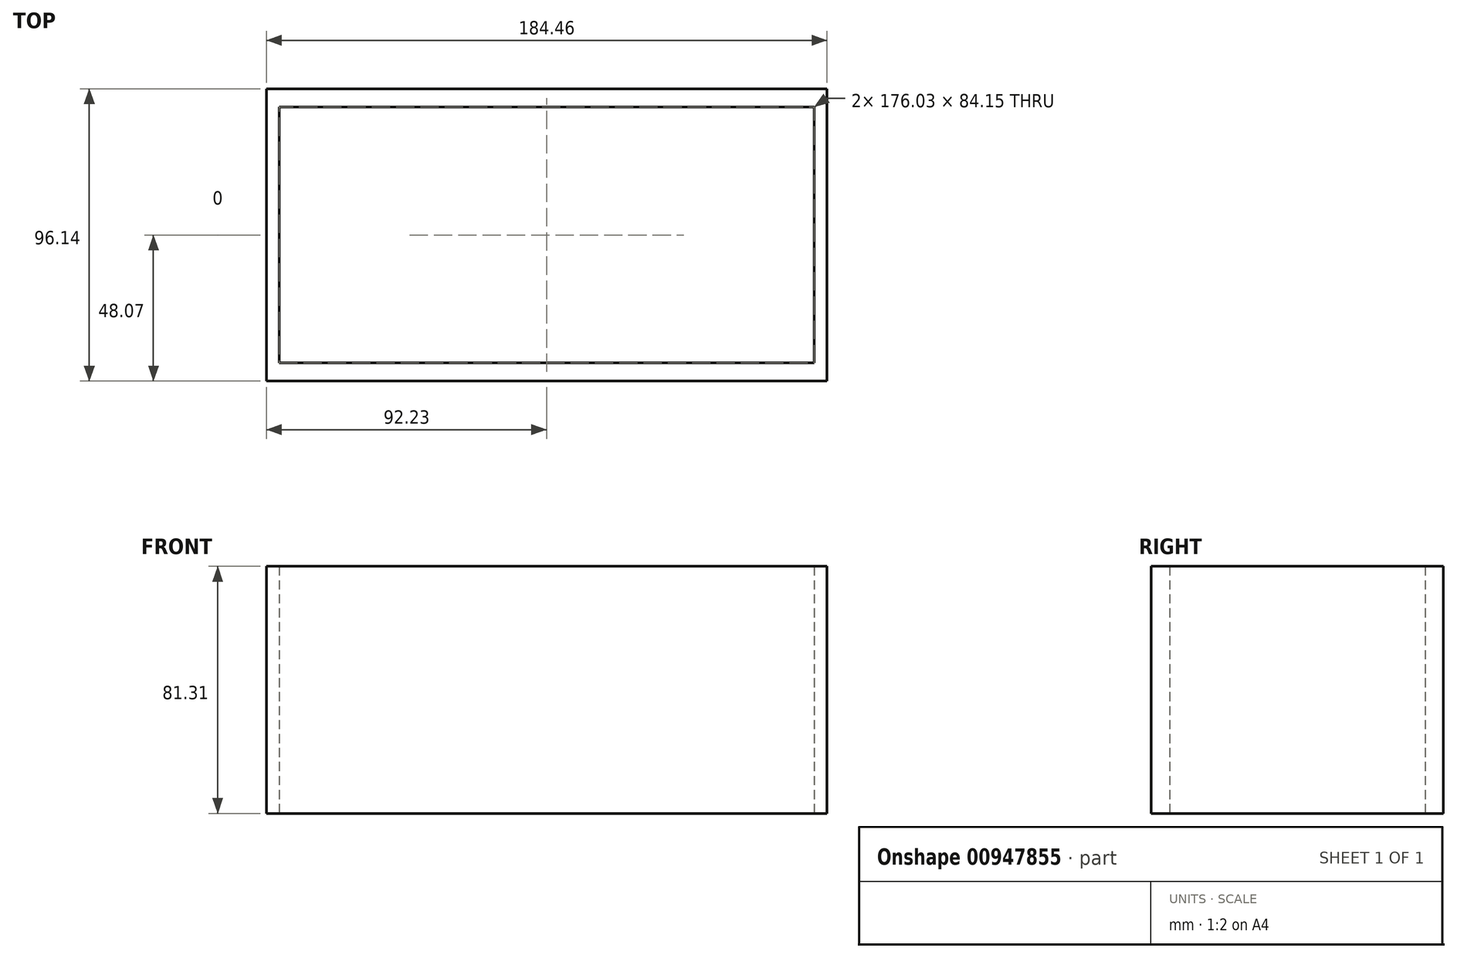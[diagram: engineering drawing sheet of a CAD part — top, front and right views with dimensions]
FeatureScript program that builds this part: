
annotation { "Feature Type Name" : "Feature", "Feature Type Description" : "" }
export const myFeature = defineFeature(function(context is Context, id is Id, definition is map)
    precondition{}
    {
        {
            var Q0;
            Q0=qCreatedBy(makeId("Top.planeOp"),FACE);
            var sketch = newSketch(context, id + "F0", { "sketchPlane" : qUnion([Q0])});
            skLineSegment(sketch, "E0.bottom", {"start": v(92.23, 48.07) * mm, "end": v(-92.23, 48.07) * mm});
            skLineSegment(sketch, "E0.top", {"start": v(92.23, -48.07) * mm, "end": v(-92.23, -48.07) * mm});
            skLineSegment(sketch, "E0.left", {"start": v(92.23, 48.07) * mm, "end": v(92.23, -48.07) * mm});
            skLineSegment(sketch, "E0.right", {"start": v(-92.23, 48.07) * mm, "end": v(-92.23, -48.07) * mm});
            skPoint(sketch, "E0.middle", {"position": v(0, 0) * mm});
            skSolve(sketch);
        }
        {
            var Q0;
            Q0 = qSketchRegion(id + "F0", true);
            var sketch = newSketch(context, id + "F1", { "sketchPlane" : qUnion([Q0])});
            skLineSegment(sketch, "E1.bottom", {"start": v(88.02, 42.08) * mm, "end": v(-88.02, 42.08) * mm});
            skLineSegment(sketch, "E1.top", {"start": v(88.02, -42.08) * mm, "end": v(-88.02, -42.08) * mm});
            skLineSegment(sketch, "E1.left", {"start": v(88.02, 42.08) * mm, "end": v(88.02, -42.08) * mm});
            skLineSegment(sketch, "E1.right", {"start": v(-88.02, 42.08) * mm, "end": v(-88.02, -42.08) * mm});
            skPoint(sketch, "E1.middle", {"position": v(0, 0) * mm});
            skSolve(sketch);
        }
        {
            var Q0;
            Q0=makeQuery(id+"F1.imprint","IMPRINT",FACE,{"disambiguationData":[TD([[makeQuery(id+"F1.imprint","IMPRINT",EDGE,{"derivedFrom":sQuery(id+"F1.wireOp",EDGE,"E1.bottom")}),-1.0]])]});
            extrude(context, id + "F2", {"entities" : qUnion([Q0]), "depth" : 81.31 * mm, "offsetDistance" : 25.4 * mm});
        }
    });
